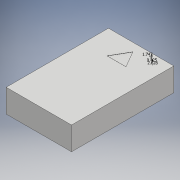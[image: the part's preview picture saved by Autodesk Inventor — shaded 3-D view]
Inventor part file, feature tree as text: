
AUTODESK INVENTOR PART (.ipt)
format: ipt  version: 2017 (Build 210142000, 142)  size: 149,504 bytes
history: native  units: mm
features: sketch x5, extrude x4, projected_geometry x2
ambient origin geometry x8: Origin, YZ Plane, XZ Plane, XY Plane, X Axis, Y Axis, Z Axis, Center Point
bodies: Solid1 (feature_tree)
feature tree (11):
  extrude  "Extrusion1"  Depth=34.5mm
  extrude  "Extrusion2"  Depth=41.0mm
  extrude  "Extrusion3"  Depth=0.1mm TaperAngle=0.0deg
  extrude  "Extrusion4"  Depth=4.0mm
  sketch  "Sketch5"  dims[d10=3.0mm d11=0.0mm d12=2.15mm d13=4.9mm d14=6.0mm d15=4.0mm d16=12.6mm d17=2.6mm d18=2.6mm d19=0.9mm d20=0.0mm d21=2.0mm d22=4.700257mm d23=2.43mm d24=4.16mm d25=2.628304mm d26=1.747164mm d27=0.425446mm]
  sketch  "Sketch1"  dims[d0=54.0mm d1=34.5mm]
  sketch  "Sketch2"  dims[d2=12.25mm d3=0.0mm d4=41.0mm]
  sketch  "Sketch3"  dims[d5=10.0mm d6=0.1mm d7=0.0mm]
  projected_geometry  "Projected Loop1"
  sketch  "Sketch4"  dims[d8=3.0mm d9=4.0mm]
  projected_geometry  "Projected Loop2"
